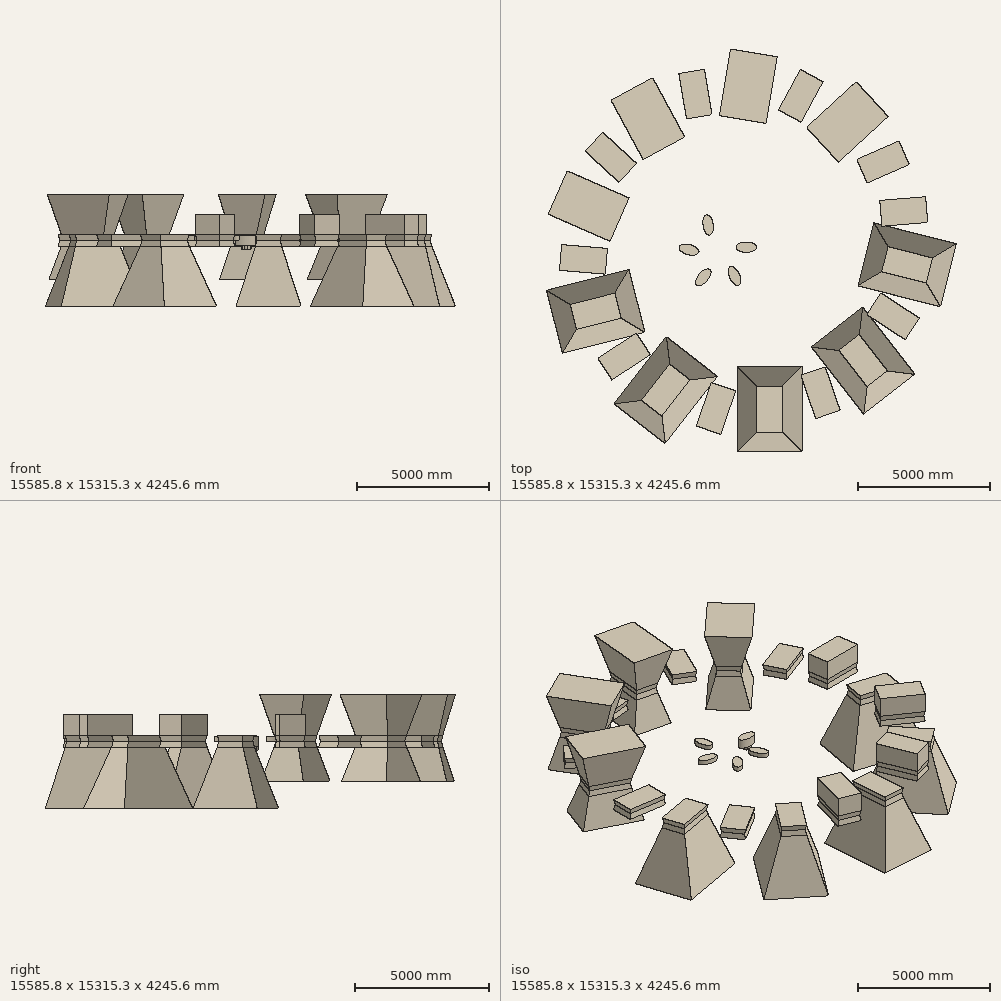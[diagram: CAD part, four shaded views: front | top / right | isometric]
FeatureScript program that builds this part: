
annotation { "Feature Type Name" : "Feature", "Feature Type Description" : "" }
export const myFeature = defineFeature(function(context is Context, id is Id, definition is map)
    precondition{}
    {
        {
            var Q0;
            Q0=qCreatedBy(makeId("Top.planeOp"),FACE);
            var sketch = newSketch(context, id + "F0", { "sketchPlane" : qUnion([Q0])});
            skEllipse(sketch, "E0", {"center": v(178.73, -29.11) * mm, "majorRadius": 60.2 * mm, "minorRadius": 26.2 * mm, "majorAxis": v(0.9, 0.44)});
            skEllipse(sketch, "E1.1.0", {"center": v(222.85, 89.16) * mm, "majorRadius": 60.2 * mm, "minorRadius": 26.2 * mm, "majorAxis": v(0.22, 0.98)});
            skEllipse(sketch, "E1.2.0", {"center": v(157.9, 197.4) * mm, "majorRadius": 60.2 * mm, "minorRadius": 26.2 * mm, "majorAxis": v(-0.62, 0.78)});
            skEllipse(sketch, "E1.3.0", {"center": v(32.77, 214.1) * mm, "majorRadius": 60.2 * mm, "minorRadius": 26.2 * mm, "majorAxis": v(-1, 0)});
            skEllipse(sketch, "E1.4.0", {"center": v(-58.3, 126.7) * mm, "majorRadius": 60.2 * mm, "minorRadius": 26.2 * mm, "majorAxis": v(-0.62, -0.78)});
            skEllipse(sketch, "E1.5.0", {"center": v(-46.74, 0.99) * mm, "majorRadius": 60.2 * mm, "minorRadius": 26.2 * mm, "majorAxis": v(0.22, -0.97)});
            skEllipse(sketch, "E1.6.0", {"center": v(58.75, -68.35) * mm, "majorRadius": 60.2 * mm, "minorRadius": 26.2 * mm, "majorAxis": v(0.9, -0.43)});
            skPoint(sketch, "E1.center", {"position": v(78, 75.84) * mm});
            skSolve(sketch);
        }
        {
            var Q0;
            Q0 = qSketchRegion(id + "F0", true);
            extrude(context, id + "F1", {"entities" : qUnion([Q0]), "depth" : 179.58 * mm, "offsetDistance" : 25.4 * mm});
        }
        {
            var Q0;
            Q0=makeQuery(id+"F1.opExtrude","CAP_FACE",FACE,{"disambiguationData":[OSD([sQuery(id+"F0.wireOp",EDGE,"E1.4.0")])],"isStart":false});
            var sketch = newSketch(context, id + "F2", { "sketchPlane" : qUnion([Q0])});
            skEllipse(sketch, "E2", {"center": v(34.27, 54.26) * mm, "majorRadius": 389.74 * mm, "minorRadius": 194.16 * mm, "majorAxis": v(1, 0)});
            skSolve(sketch);
        }
        {
            var Q0;
            Q0 = qSketchRegion(id + "F2", true);
            extrude(context, id + "F3", {"entities" : qUnion([Q0]), "depth" : 179.58 * mm, "offsetDistance" : 25.4 * mm});
        }
        {
            var Q0;
            Q0=makeQuery(id+"F3.opExtrude","CAP_FACE",FACE,{"disambiguationData":[OSD([sQuery(id+"F2.wireOp",EDGE,"E2")])],"isStart":false});
            var sketch = newSketch(context, id + "F4", { "sketchPlane" : qUnion([Q0])});
            skEllipse(sketch, "E3.0", {"center": v(34.27, 54.26) * mm, "majorRadius": 389.74 * mm, "minorRadius": 194.16 * mm, "majorAxis": v(1, 0)});
            skEllipse(sketch, "E4.1.0", {"center": v(-417.84, -1042.12) * mm, "majorRadius": 389.74 * mm, "minorRadius": 194.16 * mm, "majorAxis": v(0.42, -0.9)});
            skEllipse(sketch, "E4.2.0", {"center": v(-1602.7, -1093.28) * mm, "majorRadius": 389.74 * mm, "minorRadius": 194.16 * mm, "majorAxis": v(-0.65, -0.76)});
            skEllipse(sketch, "E4.3.0", {"center": v(-2147.63, -39.95) * mm, "majorRadius": 389.74 * mm, "minorRadius": 194.16 * mm, "majorAxis": v(-0.96, 0.26)});
            skEllipse(sketch, "E4.4.0", {"center": v(-1421.36, 897.6) * mm, "majorRadius": 389.74 * mm, "minorRadius": 194.16 * mm, "majorAxis": v(-0.17, 0.99)});
            skPoint(sketch, "E4.center", {"position": v(-1050.33, -139.9) * mm});
            skLineSegment(sketch, "E4.anchor1", {"start": v(-1050.33, -139.9) * mm, "end": v(34.27, 54.26) * mm, "construction": true});
            skLineSegment(sketch, "E4.anchor2", {"start": v(-1050.33, -139.9) * mm, "end": v(-1421.36, 897.6) * mm, "construction": true});
            skSolve(sketch);
        }
        {
            var Q0;
            Q0 = qSketchRegion(id + "F4", true);
            extrude(context, id + "F5", {"entities" : qUnion([Q0]), "operationType" : NewBodyOperationType.ADD, "depth" : 179.58 * mm, "offsetDistance" : 25.4 * mm});
        }
        {
            var Q0;
            Q0=makeQuery(id+"F5.opExtrude","CAP_FACE",FACE,{"disambiguationData":[OSD([sQuery(id+"F4.wireOp",EDGE,"E4.1.0")])],"isStart":true});
            var sketch = newSketch(context, id + "F6", { "sketchPlane" : qUnion([Q0])});
            skLineSegment(sketch, "E5.bottom", {"start": v(1358.5, 5279.95) * mm, "end": v(467.98, 5279.95) * mm});
            skLineSegment(sketch, "E5.top", {"start": v(1358.5, 6936.82) * mm, "end": v(467.98, 6936.82) * mm});
            skLineSegment(sketch, "E5.left", {"start": v(1358.5, 5279.95) * mm, "end": v(1358.5, 6936.82) * mm});
            skLineSegment(sketch, "E5.right", {"start": v(467.98, 5279.95) * mm, "end": v(467.98, 6936.82) * mm});
            skLineSegment(sketch, "E6.1.0", {"start": v(-429.5, 5434.98) * mm, "end": v(-1271.77, 5145.82) * mm});
            skLineSegment(sketch, "E6.1.1", {"start": v(-1271.77, 5145.82) * mm, "end": v(-1809.76, 6712.92) * mm});
            skLineSegment(sketch, "E6.1.2", {"start": v(-967.49, 7002.07) * mm, "end": v(-1809.76, 6712.92) * mm});
            skLineSegment(sketch, "E6.1.3", {"start": v(-429.5, 5434.98) * mm, "end": v(-967.49, 7002.07) * mm});
            skLineSegment(sketch, "E6.2.0", {"start": v(-2170.96, 5001.03) * mm, "end": v(-2873.71, 4454.07) * mm});
            skLineSegment(sketch, "E6.2.1", {"start": v(-2873.71, 4454.07) * mm, "end": v(-3891.38, 5761.57) * mm});
            skLineSegment(sketch, "E6.2.2", {"start": v(-3188.64, 6308.54) * mm, "end": v(-3891.38, 5761.57) * mm});
            skLineSegment(sketch, "E6.2.3", {"start": v(-2170.96, 5001.03) * mm, "end": v(-3188.64, 6308.54) * mm});
            skLineSegment(sketch, "E6.3.0", {"start": v(-3677.17, 4025.15) * mm, "end": v(-4164.24, 3279.64) * mm});
            skLineSegment(sketch, "E6.3.1", {"start": v(-4164.24, 3279.64) * mm, "end": v(-5551.31, 4185.86) * mm});
            skLineSegment(sketch, "E6.3.2", {"start": v(-5064.25, 4931.38) * mm, "end": v(-5551.31, 4185.86) * mm});
            skLineSegment(sketch, "E6.3.3", {"start": v(-3677.17, 4025.15) * mm, "end": v(-5064.25, 4931.38) * mm});
            skLineSegment(sketch, "E6.4.0", {"start": v(-4784.9, 2613.08) * mm, "end": v(-5003.5, 1749.81) * mm});
            skLineSegment(sketch, "E6.4.1", {"start": v(-5003.5, 1749.81) * mm, "end": v(-6609.68, 2156.55) * mm});
            skLineSegment(sketch, "E6.4.2", {"start": v(-6391.07, 3019.82) * mm, "end": v(-6609.68, 2156.55) * mm});
            skLineSegment(sketch, "E6.4.3", {"start": v(-4784.9, 2613.08) * mm, "end": v(-6391.07, 3019.82) * mm});
            skLineSegment(sketch, "E6.5.0", {"start": v(-5374.1, 917.85) * mm, "end": v(-5300.56, 30.37) * mm});
            skLineSegment(sketch, "E6.5.1", {"start": v(-5300.56, 30.37) * mm, "end": v(-6951.78, -106.45) * mm});
            skLineSegment(sketch, "E6.5.2", {"start": v(-7025.32, 781.02) * mm, "end": v(-6951.78, -106.45) * mm});
            skLineSegment(sketch, "E6.5.3", {"start": v(-5374.1, 917.85) * mm, "end": v(-7025.32, 781.02) * mm});
            skLineSegment(sketch, "E6.6.0", {"start": v(-5380.94, -876.85) * mm, "end": v(-5023.23, -1692.37) * mm});
            skLineSegment(sketch, "E6.6.1", {"start": v(-5023.23, -1692.37) * mm, "end": v(-6540.55, -2357.92) * mm});
            skLineSegment(sketch, "E6.6.2", {"start": v(-6898.26, -1542.41) * mm, "end": v(-6540.55, -2357.92) * mm});
            skLineSegment(sketch, "E6.6.3", {"start": v(-5380.94, -876.85) * mm, "end": v(-6898.26, -1542.41) * mm});
            skLineSegment(sketch, "E6.7.0", {"start": v(-4804.68, -2576.53) * mm, "end": v(-4201.54, -3231.7) * mm});
            skLineSegment(sketch, "E6.7.1", {"start": v(-4201.54, -3231.7) * mm, "end": v(-5420.54, -4353.88) * mm});
            skLineSegment(sketch, "E6.7.2", {"start": v(-6023.68, -3698.7) * mm, "end": v(-5420.54, -4353.88) * mm});
            skLineSegment(sketch, "E6.7.3", {"start": v(-4804.68, -2576.53) * mm, "end": v(-6023.68, -3698.7) * mm});
            skLineSegment(sketch, "E6.8.0", {"start": v(-3707.75, -3997) * mm, "end": v(-2924.56, -4420.84) * mm});
            skLineSegment(sketch, "E6.8.1", {"start": v(-2924.56, -4420.84) * mm, "end": v(-3713.14, -5878.02) * mm});
            skLineSegment(sketch, "E6.8.2", {"start": v(-4496.33, -5454.18) * mm, "end": v(-3713.14, -5878.02) * mm});
            skLineSegment(sketch, "E6.8.3", {"start": v(-3707.75, -3997) * mm, "end": v(-4496.33, -5454.18) * mm});
            skLineSegment(sketch, "E6.9.0", {"start": v(-2209.03, -4984.34) * mm, "end": v(-1330.65, -5130.91) * mm});
            skLineSegment(sketch, "E6.9.1", {"start": v(-1330.65, -5130.91) * mm, "end": v(-1603.36, -6765.19) * mm});
            skLineSegment(sketch, "E6.9.2", {"start": v(-2481.74, -6618.61) * mm, "end": v(-1603.36, -6765.19) * mm});
            skLineSegment(sketch, "E6.9.3", {"start": v(-2209.03, -4984.34) * mm, "end": v(-2481.74, -6618.61) * mm});
            skLineSegment(sketch, "E6.10.0", {"start": v(-470.92, -5431.54) * mm, "end": v(407.45, -5284.97) * mm});
            skLineSegment(sketch, "E6.10.1", {"start": v(407.45, -5284.97) * mm, "end": v(680.16, -6919.24) * mm});
            skLineSegment(sketch, "E6.10.2", {"start": v(-198.21, -7065.82) * mm, "end": v(680.16, -6919.24) * mm});
            skLineSegment(sketch, "E6.10.3", {"start": v(-470.92, -5431.54) * mm, "end": v(-198.21, -7065.82) * mm});
            skLineSegment(sketch, "E6.11.0", {"start": v(1318.21, -5290.16) * mm, "end": v(2101.4, -4866.32) * mm});
            skLineSegment(sketch, "E6.11.1", {"start": v(2101.4, -4866.32) * mm, "end": v(2889.99, -6323.5) * mm});
            skLineSegment(sketch, "E6.11.2", {"start": v(2106.8, -6747.33) * mm, "end": v(2889.99, -6323.5) * mm});
            skLineSegment(sketch, "E6.11.3", {"start": v(1318.21, -5290.16) * mm, "end": v(2106.8, -6747.33) * mm});
            skLineSegment(sketch, "E6.12.0", {"start": v(2964.5, -4575.5) * mm, "end": v(3567.63, -3920.32) * mm});
            skLineSegment(sketch, "E6.12.1", {"start": v(3567.63, -3920.32) * mm, "end": v(4786.63, -5042.49) * mm});
            skLineSegment(sketch, "E6.12.2", {"start": v(4183.5, -5697.67) * mm, "end": v(4786.63, -5042.49) * mm});
            skLineSegment(sketch, "E6.12.3", {"start": v(2964.5, -4575.5) * mm, "end": v(4183.5, -5697.67) * mm});
            skLineSegment(sketch, "E6.13.0", {"start": v(4289.54, -3365.01) * mm, "end": v(4647.25, -2549.5) * mm});
            skLineSegment(sketch, "E6.13.1", {"start": v(4647.25, -2549.5) * mm, "end": v(6164.57, -3215.06) * mm});
            skLineSegment(sketch, "E6.13.2", {"start": v(5806.85, -4030.57) * mm, "end": v(6164.57, -3215.06) * mm});
            skLineSegment(sketch, "E6.13.3", {"start": v(4289.54, -3365.01) * mm, "end": v(5806.85, -4030.57) * mm});
            skLineSegment(sketch, "E6.14.0", {"start": v(5149.74, -1789.88) * mm, "end": v(5223.27, -902.4) * mm});
            skLineSegment(sketch, "E6.14.1", {"start": v(5223.27, -902.4) * mm, "end": v(6874.49, -1039.22) * mm});
            skLineSegment(sketch, "E6.14.2", {"start": v(6800.95, -1926.7) * mm, "end": v(6874.49, -1039.22) * mm});
            skLineSegment(sketch, "E6.14.3", {"start": v(5149.74, -1789.88) * mm, "end": v(6800.95, -1926.7) * mm});
            skLineSegment(sketch, "E6.15.0", {"start": v(5451.88, -20.78) * mm, "end": v(5233.27, 842.49) * mm});
            skLineSegment(sketch, "E6.15.1", {"start": v(5233.27, 842.49) * mm, "end": v(6839.44, 1249.23) * mm});
            skLineSegment(sketch, "E6.15.2", {"start": v(7058.05, 385.96) * mm, "end": v(6839.44, 1249.23) * mm});
            skLineSegment(sketch, "E6.15.3", {"start": v(5451.88, -20.78) * mm, "end": v(7058.05, 385.96) * mm});
            skLineSegment(sketch, "E6.16.0", {"start": v(5163.23, 1750.57) * mm, "end": v(4676.16, 2496.08) * mm});
            skLineSegment(sketch, "E6.16.1", {"start": v(4676.16, 2496.08) * mm, "end": v(6063.24, 3402.3) * mm});
            skLineSegment(sketch, "E6.16.2", {"start": v(6550.3, 2656.8) * mm, "end": v(6063.24, 3402.3) * mm});
            skLineSegment(sketch, "E6.16.3", {"start": v(5163.23, 1750.57) * mm, "end": v(6550.3, 2656.8) * mm});
            skLineSegment(sketch, "E6.17.0", {"start": v(4315.06, 3332.22) * mm, "end": v(3612.32, 3879.18) * mm});
            skLineSegment(sketch, "E6.17.1", {"start": v(3612.32, 3879.18) * mm, "end": v(4630, 5186.69) * mm});
            skLineSegment(sketch, "E6.17.2", {"start": v(5332.74, 4639.72) * mm, "end": v(4630, 5186.69) * mm});
            skLineSegment(sketch, "E6.17.3", {"start": v(4315.06, 3332.22) * mm, "end": v(5332.74, 4639.72) * mm});
            skLineSegment(sketch, "E6.18.0", {"start": v(2999.3, 4552.77) * mm, "end": v(2157.02, 4841.92) * mm});
            skLineSegment(sketch, "E6.18.1", {"start": v(2157.02, 4841.92) * mm, "end": v(2695, 6409.01) * mm});
            skLineSegment(sketch, "E6.18.2", {"start": v(3537.28, 6119.86) * mm, "end": v(2695, 6409.01) * mm});
            skLineSegment(sketch, "E6.18.3", {"start": v(2999.3, 4552.77) * mm, "end": v(3537.28, 6119.86) * mm});
            skPoint(sketch, "E6.center", {"position": v(0, 0) * mm});
            skSolve(sketch);
        }
        {
            var Q0;
            Q0 = qSketchRegion(id + "F6", true);
            extrude(context, id + "F7", {"entities" : qUnion([Q0]), "endBound" : BoundingType.SYMMETRIC, "depth" : 431.8 * mm, "offsetDistance" : 25.4 * mm, "hasDraft" : true, "draftAngle" : 12 * degree});
        }
        {
            var Q0;
            Q0=makeQuery(id+"F7.opExtrude","CAP_FACE",FACE,{"disambiguationData":[OSD([sQuery(id+"F6.wireOp",EDGE,"E6.14.0"),sQuery(id+"F6.wireOp",EDGE,"E6.14.1"),sQuery(id+"F6.wireOp",EDGE,"E6.14.2"),sQuery(id+"F6.wireOp",EDGE,"E6.14.3")])],"isStart":true});
            var Q1;
            Q1=makeQuery(id+"F7.opExtrude","CAP_FACE",FACE,{"disambiguationData":[OSD([sQuery(id+"F6.wireOp",EDGE,"E6.16.0"),sQuery(id+"F6.wireOp",EDGE,"E6.16.1"),sQuery(id+"F6.wireOp",EDGE,"E6.16.2"),sQuery(id+"F6.wireOp",EDGE,"E6.16.3")])],"isStart":true});
            var Q2;
            Q2=makeQuery(id+"F7.opExtrude","CAP_FACE",FACE,{"disambiguationData":[OSD([sQuery(id+"F6.wireOp",EDGE,"E6.18.0"),sQuery(id+"F6.wireOp",EDGE,"E6.18.1"),sQuery(id+"F6.wireOp",EDGE,"E6.18.2"),sQuery(id+"F6.wireOp",EDGE,"E6.18.3")])],"isStart":true});
            var Q3;
            Q3=makeQuery(id+"F7.opExtrude","CAP_FACE",FACE,{"disambiguationData":[OSD([sQuery(id+"F6.wireOp",EDGE,"E6.1.0"),sQuery(id+"F6.wireOp",EDGE,"E6.1.1"),sQuery(id+"F6.wireOp",EDGE,"E6.1.2"),sQuery(id+"F6.wireOp",EDGE,"E6.1.3")])],"isStart":true});
            extrude(context, id + "F8", {"entities" : qUnion([Q0, Q1, Q2, Q3]), "depth" : 769.62 * mm, "offsetDistance" : 25.4 * mm});
        }
        {
            var Q0;
            Q0=makeQuery(id+"F7.opExtrude","CAP_FACE",FACE,{"disambiguationData":[OSD([sQuery(id+"F6.wireOp",EDGE,"E6.12.0"),sQuery(id+"F6.wireOp",EDGE,"E6.12.1"),sQuery(id+"F6.wireOp",EDGE,"E6.12.2"),sQuery(id+"F6.wireOp",EDGE,"E6.12.3")])],"isStart":true});
            var Q1;
            Q1=makeQuery(id+"F7.opExtrude","CAP_FACE",FACE,{"disambiguationData":[OSD([sQuery(id+"F6.wireOp",EDGE,"E6.10.0"),sQuery(id+"F6.wireOp",EDGE,"E6.10.1"),sQuery(id+"F6.wireOp",EDGE,"E6.10.2"),sQuery(id+"F6.wireOp",EDGE,"E6.10.3")])],"isStart":true});
            var Q2;
            Q2=makeQuery(id+"F7.opExtrude","CAP_FACE",FACE,{"disambiguationData":[OSD([sQuery(id+"F6.wireOp",EDGE,"E6.8.0"),sQuery(id+"F6.wireOp",EDGE,"E6.8.1"),sQuery(id+"F6.wireOp",EDGE,"E6.8.2"),sQuery(id+"F6.wireOp",EDGE,"E6.8.3")])],"isStart":true});
            var Q3;
            Q3=makeQuery(id+"F7.opExtrude","CAP_FACE",FACE,{"disambiguationData":[OSD([sQuery(id+"F6.wireOp",EDGE,"E6.6.0"),sQuery(id+"F6.wireOp",EDGE,"E6.6.1"),sQuery(id+"F6.wireOp",EDGE,"E6.6.2"),sQuery(id+"F6.wireOp",EDGE,"E6.6.3")])],"isStart":true});
            extrude(context, id + "F9", {"entities" : qUnion([Q0, Q1, Q2, Q3]), "depth" : 1525.52 * mm, "offsetDistance" : 25.4 * mm, "hasDraft" : true, "draftAngle" : 15 * degree});
        }
        {
            var Q0;
            Q0=makeQuery(id+"F7.opExtrude","CAP_FACE",FACE,{"disambiguationData":[OSD([sQuery(id+"F6.wireOp",EDGE,"E6.6.0"),sQuery(id+"F6.wireOp",EDGE,"E6.6.1"),sQuery(id+"F6.wireOp",EDGE,"E6.6.2"),sQuery(id+"F6.wireOp",EDGE,"E6.6.3")])],"isStart":false});
            var sketch = newSketch(context, id + "F10", { "sketchPlane" : qUnion([Q0])});
            skCircle(sketch, "E7", {"center": v(0, 0) * mm, "radius": 6148.23 * mm});
            skSolve(sketch);
        }
        {
            var Q0;
            {var subQ5=makeQuery(id+"F7.opExtrude","CAP_EDGE",EDGE,{"disambiguationData":[OSD([sQuery(id+"F6.wireOp",EDGE,"E6.6.2")])],"isStart":false});Q0=makeQuery(id+"F10.imprint","IMPRINT",FACE,{"disambiguationData":[TD([[makeQuery(id+"F10.imprint","IMPRINT",EDGE,{"derivedFrom":subQ5}),1.0]])]});}
            var Q1;
            {var subQ5=makeQuery(id+"F7.opExtrude","CAP_EDGE",EDGE,{"disambiguationData":[OSD([sQuery(id+"F6.wireOp",EDGE,"E6.6.0")])],"isStart":false});Q1=makeQuery(id+"F10.imprint","IMPRINT",FACE,{"disambiguationData":[TD([[makeQuery(id+"F10.imprint","IMPRINT",EDGE,{"derivedFrom":subQ5}),-1.0]])]});}
            var Q2;
            Q2=makeQuery(id+"F7.opExtrude","CAP_FACE",FACE,{"disambiguationData":[OSD([sQuery(id+"F6.wireOp",EDGE,"E6.8.0"),sQuery(id+"F6.wireOp",EDGE,"E6.8.1"),sQuery(id+"F6.wireOp",EDGE,"E6.8.2"),sQuery(id+"F6.wireOp",EDGE,"E6.8.3")])],"isStart":false});
            var Q3;
            Q3=makeQuery(id+"F7.opExtrude","CAP_FACE",FACE,{"disambiguationData":[OSD([sQuery(id+"F6.wireOp",EDGE,"E6.10.0"),sQuery(id+"F6.wireOp",EDGE,"E6.10.1"),sQuery(id+"F6.wireOp",EDGE,"E6.10.2"),sQuery(id+"F6.wireOp",EDGE,"E6.10.3")])],"isStart":false});
            var Q4;
            Q4=makeQuery(id+"F7.opExtrude","CAP_FACE",FACE,{"disambiguationData":[OSD([sQuery(id+"F6.wireOp",EDGE,"E6.12.0"),sQuery(id+"F6.wireOp",EDGE,"E6.12.1"),sQuery(id+"F6.wireOp",EDGE,"E6.12.2"),sQuery(id+"F6.wireOp",EDGE,"E6.12.3")])],"isStart":false});
            extrude(context, id + "F11", {"entities" : qUnion([Q0, Q1, Q2, Q3, Q4]), "depth" : 1271.27 * mm, "offsetDistance" : 25.4 * mm, "hasDraft" : true, "draftAngle" : 16 * degree});
        }
        {
            var Q0;
            Q0=makeQuery(id+"F7.opExtrude","CAP_FACE",FACE,{"disambiguationData":[OSD([sQuery(id+"F6.wireOp",EDGE,"E6.15.0"),sQuery(id+"F6.wireOp",EDGE,"E6.15.1"),sQuery(id+"F6.wireOp",EDGE,"E6.15.2"),sQuery(id+"F6.wireOp",EDGE,"E6.15.3")])],"isStart":false});
            var Q1;
            Q1=makeQuery(id+"F7.opExtrude","CAP_FACE",FACE,{"disambiguationData":[OSD([sQuery(id+"F6.wireOp",EDGE,"E6.17.0"),sQuery(id+"F6.wireOp",EDGE,"E6.17.1"),sQuery(id+"F6.wireOp",EDGE,"E6.17.2"),sQuery(id+"F6.wireOp",EDGE,"E6.17.3")])],"isStart":false});
            var Q2;
            Q2=makeQuery(id+"F7.opExtrude","CAP_FACE",FACE,{"disambiguationData":[OSD([sQuery(id+"F6.wireOp",EDGE,"E5.bottom"),sQuery(id+"F6.wireOp",EDGE,"E5.top"),sQuery(id+"F6.wireOp",EDGE,"E5.left"),sQuery(id+"F6.wireOp",EDGE,"E5.right")])],"isStart":false});
            var Q3;
            Q3=makeQuery(id+"F7.opExtrude","CAP_FACE",FACE,{"disambiguationData":[OSD([sQuery(id+"F6.wireOp",EDGE,"E6.2.0"),sQuery(id+"F6.wireOp",EDGE,"E6.2.1"),sQuery(id+"F6.wireOp",EDGE,"E6.2.2"),sQuery(id+"F6.wireOp",EDGE,"E6.2.3")])],"isStart":false});
            var Q4;
            Q4=makeQuery(id+"F7.opExtrude","CAP_FACE",FACE,{"disambiguationData":[OSD([sQuery(id+"F6.wireOp",EDGE,"E6.4.0"),sQuery(id+"F6.wireOp",EDGE,"E6.4.1"),sQuery(id+"F6.wireOp",EDGE,"E6.4.2"),sQuery(id+"F6.wireOp",EDGE,"E6.4.3")])],"isStart":false});
            extrude(context, id + "F12", {"entities" : qUnion([Q0, Q1, Q2, Q3, Q4]), "depth" : 2288.29 * mm, "offsetDistance" : 25.4 * mm, "hasDraft" : true, "draftAngle" : 18 * degree});
        }
    });
